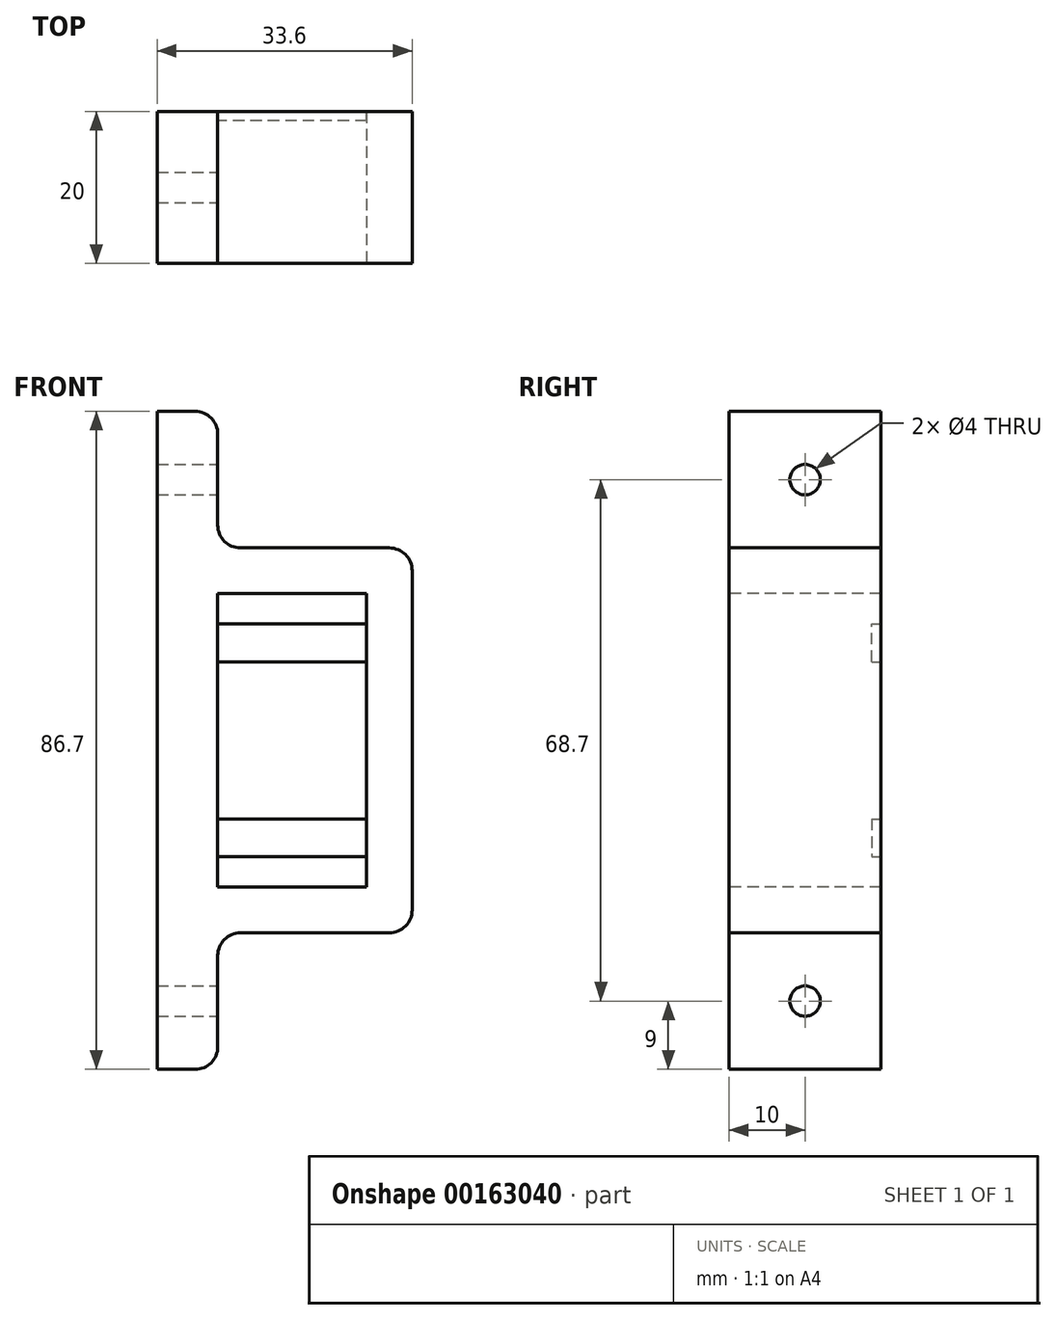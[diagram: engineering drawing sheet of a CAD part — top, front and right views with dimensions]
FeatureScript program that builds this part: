
annotation { "Feature Type Name" : "Feature", "Feature Type Description" : "" }
export const myFeature = defineFeature(function(context is Context, id is Id, definition is map)
    precondition{}
    {
        {
            var Q0;
            Q0=qCreatedBy(makeId("Front.planeOp"),FACE);
            var sketch = newSketch(context, id + "F0", { "sketchPlane" : qUnion([Q0])});
            skLineSegment(sketch, "E0.bottom", {"start": v(13.8, -25.35) * mm, "end": v(-5.8, -25.35) * mm});
            skLineSegment(sketch, "E0.top", {"start": v(13.8, 25.35) * mm, "end": v(-5.8, 25.35) * mm});
            skLineSegment(sketch, "E0.left", {"start": v(16.8, -22.35) * mm, "end": v(16.8, 22.35) * mm});
            skLineSegment(sketch, "E0.right", {"start": v(-16.8, -25.35) * mm, "end": v(-16.8, 25.35) * mm});
            skPoint(sketch, "E0.middle", {"position": v(0, 0) * mm});
            skLineSegment(sketch, "E1.top", {"start": v(-16.8, 43.35) * mm, "end": v(-11.8, 43.35) * mm});
            skLineSegment(sketch, "E1.left", {"start": v(-16.8, 25.35) * mm, "end": v(-16.8, 43.35) * mm});
            skLineSegment(sketch, "E1.right", {"start": v(-8.8, 28.35) * mm, "end": v(-8.8, 40.35) * mm});
            skLineSegment(sketch, "E2.MirrorCS", {"start": v(-16.8, -25.35) * mm, "end": v(-16.8, -43.35) * mm});
            skLineSegment(sketch, "E3.MirrorCS", {"start": v(-16.8, -43.35) * mm, "end": v(-11.8, -43.35) * mm});
            skLineSegment(sketch, "E4.MirrorCS", {"start": v(-8.8, -28.35) * mm, "end": v(-8.8, -40.35) * mm});
            skPoint(sketch, "E5.visualSharp", {"position": v(16.8, 25.35) * mm});
            skArc(sketch, "E5.filletArc", {"start": v(16.8, 22.35) * mm, "mid": v(15.92, 24.47) * mm, "end": v(13.8, 25.35) * mm});
            skPoint(sketch, "E6.visualSharp", {"position": v(16.8, -25.35) * mm});
            skArc(sketch, "E6.filletArc", {"start": v(13.8, -25.35) * mm, "mid": v(15.92, -24.47) * mm, "end": v(16.8, -22.35) * mm});
            skPoint(sketch, "E7.visualSharp", {"position": v(-8.8, -25.35) * mm});
            skArc(sketch, "E7.filletArc", {"start": v(-5.8, -25.35) * mm, "mid": v(-7.92, -26.23) * mm, "end": v(-8.8, -28.35) * mm});
            skPoint(sketch, "E8.visualSharp", {"position": v(-8.8, -43.35) * mm});
            skArc(sketch, "E8.filletArc", {"start": v(-11.8, -43.35) * mm, "mid": v(-9.68, -42.47) * mm, "end": v(-8.8, -40.35) * mm});
            skPoint(sketch, "E9.visualSharp", {"position": v(-8.8, 43.35) * mm});
            skArc(sketch, "E9.filletArc", {"start": v(-8.8, 40.35) * mm, "mid": v(-9.68, 42.47) * mm, "end": v(-11.8, 43.35) * mm});
            skPoint(sketch, "E10.visualSharp", {"position": v(-8.8, 25.35) * mm});
            skArc(sketch, "E10.filletArc", {"start": v(-8.8, 28.35) * mm, "mid": v(-7.92, 26.23) * mm, "end": v(-5.8, 25.35) * mm});
            skSolve(sketch);
        }
        {
            var Q0;
            Q0=makeQuery(id+"F0.imprint","IMPRINT",FACE,{"disambiguationData":[TD([[makeQuery(id+"F0.imprint","IMPRINT",EDGE,{"derivedFrom":sQuery(id+"F0.wireOp",EDGE,"E0.bottom")}),-1.0]])]});
            extrude(context, id + "F1", {"entities" : qUnion([Q0]), "depth" : 20 * mm});
        }
        {
            var Q0;
            Q0=makeQuery(id+"F1.opExtrude","CAP_FACE",FACE,{"disambiguationData":[OSD([sQuery(id+"F0.wireOp",EDGE,"E0.bottom"),sQuery(id+"F0.wireOp",EDGE,"E0.top"),sQuery(id+"F0.wireOp",EDGE,"E0.left"),sQuery(id+"F0.wireOp",EDGE,"E0.right"),sQuery(id+"F0.wireOp",EDGE,"E1.top"),sQuery(id+"F0.wireOp",EDGE,"E1.left"),sQuery(id+"F0.wireOp",EDGE,"E1.right"),sQuery(id+"F0.wireOp",EDGE,"E2.MirrorCS"),sQuery(id+"F0.wireOp",EDGE,"E3.MirrorCS"),sQuery(id+"F0.wireOp",EDGE,"E4.MirrorCS"),sQuery(id+"F0.wireOp",EDGE,"E5.filletArc"),sQuery(id+"F0.wireOp",EDGE,"E6.filletArc"),sQuery(id+"F0.wireOp",EDGE,"E7.filletArc"),sQuery(id+"F0.wireOp",EDGE,"E8.filletArc"),sQuery(id+"F0.wireOp",EDGE,"E9.filletArc"),sQuery(id+"F0.wireOp",EDGE,"E10.filletArc")])],"isStart":false});
            var sketch = newSketch(context, id + "F2", { "sketchPlane" : qUnion([Q0])});
            skLineSegment(sketch, "E11.bottom", {"start": v(-8.8, 19.35) * mm, "end": v(10.8, 19.35) * mm});
            skLineSegment(sketch, "E11.top", {"start": v(-8.8, -19.35) * mm, "end": v(10.8, -19.35) * mm});
            skLineSegment(sketch, "E11.left", {"start": v(-8.8, 19.35) * mm, "end": v(-8.8, -19.35) * mm});
            skLineSegment(sketch, "E11.right", {"start": v(10.8, 19.35) * mm, "end": v(10.8, -19.35) * mm});
            skSolve(sketch);
        }
        {
            var Q0;
            Q0 = qSketchRegion(id + "F2", true);
            extrude(context, id + "F3", {"entities" : qUnion([Q0]), "operationType" : NewBodyOperationType.REMOVE, "oppositeDirection" : true, "depth" : 25 * mm});
        }
        {
            var Q0;
            Q0=makeQuery(id+"F1.opExtrude","SWEPT_FACE",FACE,{"disambiguationData":[OSD([sQuery(id+"F0.wireOp",EDGE,"E1.right")])]});
            var sketch = newSketch(context, id + "F4", { "sketchPlane" : qUnion([Q0])});
            skLineSegment(sketch, "E12", {"start": v(-20, 28.35) * mm, "end": v(0, 40.35) * mm, "construction": true});
            skLineSegment(sketch, "E13", {"start": v(-20, 40.35) * mm, "end": v(0, 28.35) * mm, "construction": true});
            skCircle(sketch, "E14", {"center": v(-10, 34.35) * mm, "radius": 2 * mm});
            skCircle(sketch, "E15.MirrorC", {"center": v(-10, -34.35) * mm, "radius": 2 * mm});
            skSolve(sketch);
        }
        {
            var Q0;
            Q0 = qSketchRegion(id + "F4", true);
            extrude(context, id + "F5", {"entities" : qUnion([Q0]), "operationType" : NewBodyOperationType.REMOVE, "oppositeDirection" : true, "depth" : 25 * mm});
        }
        {
            var Q0;
            Q0=makeQuery(id+"F3.boolean.opBoolean","COPY",FACE,{"derivedFrom":makeQuery(id+"F3.opExtrude","SWEPT_FACE",FACE,{"disambiguationData":[OSD([sQuery(id+"F2.wireOp",EDGE,"E11.left")])]})});
            var sketch = newSketch(context, id + "F6", { "sketchPlane" : qUnion([Q0])});
            skLineSegment(sketch, "E16.bottom", {"start": v(0, 15.35) * mm, "end": v(-1.2, 15.35) * mm});
            skLineSegment(sketch, "E16.top", {"start": v(0, 10.35) * mm, "end": v(-1.2, 10.35) * mm});
            skLineSegment(sketch, "E16.left", {"start": v(0, 15.35) * mm, "end": v(0, 10.35) * mm});
            skLineSegment(sketch, "E16.right", {"start": v(-1.2, 15.35) * mm, "end": v(-1.2, 10.35) * mm});
            skLineSegment(sketch, "E17.MirrorCS", {"start": v(0, -15.35) * mm, "end": v(0, -10.35) * mm});
            skLineSegment(sketch, "E18.MirrorCS", {"start": v(0, -10.35) * mm, "end": v(-1.2, -10.35) * mm});
            skLineSegment(sketch, "E19.MirrorCS", {"start": v(0, -15.35) * mm, "end": v(-1.2, -15.35) * mm});
            skLineSegment(sketch, "E20.MirrorCS", {"start": v(-1.2, -15.35) * mm, "end": v(-1.2, -10.35) * mm});
            skSolve(sketch);
        }
        {
            var Q0;
            Q0 = qSketchRegion(id + "F6", true);
            extrude(context, id + "F7", {"entities" : qUnion([Q0]), "operationType" : NewBodyOperationType.ADD, "endBound" : BoundingType.UP_TO_NEXT, "depth" : 2 * mm});
        }
    });
